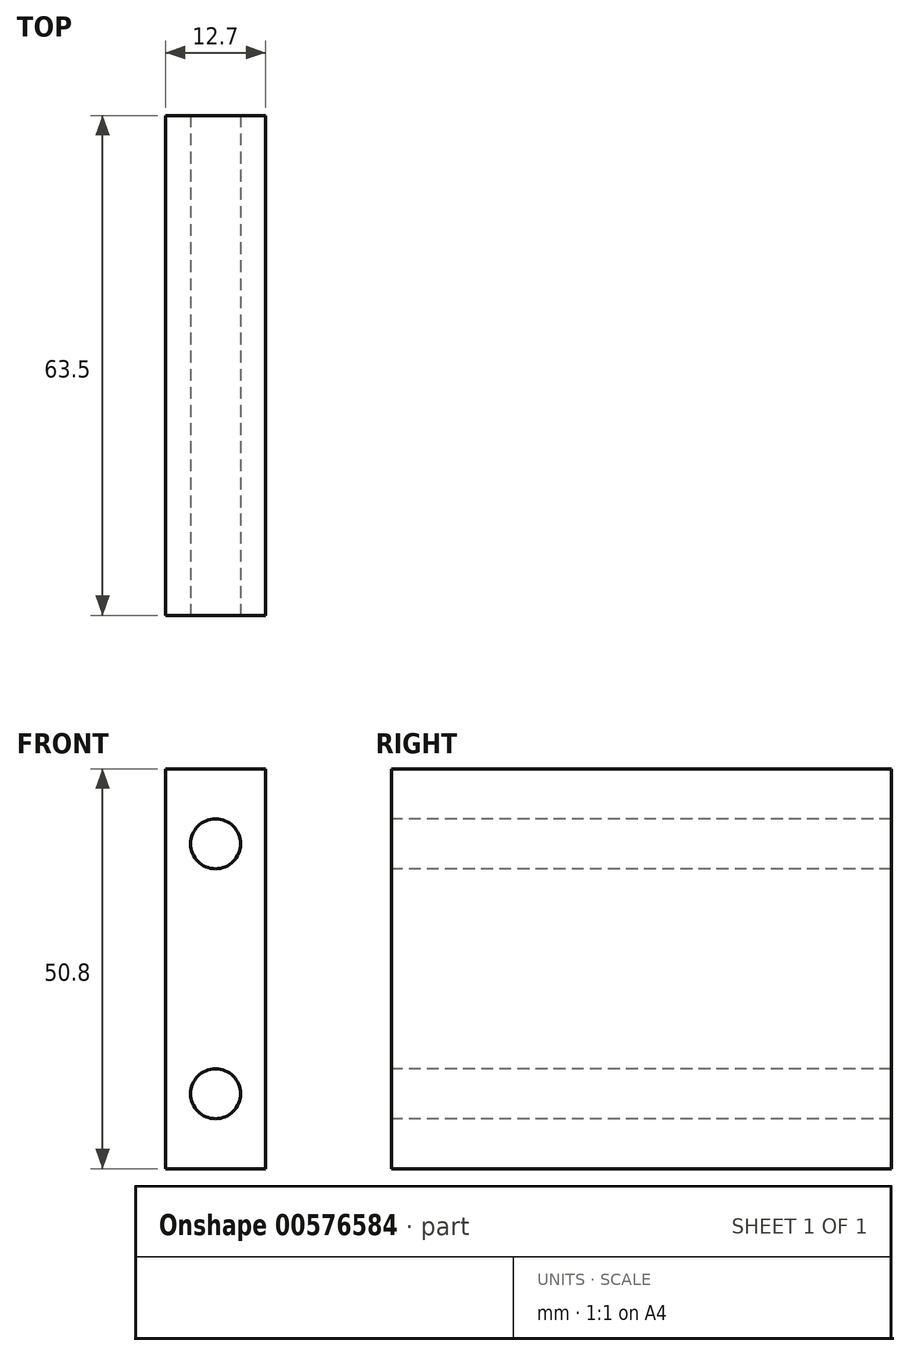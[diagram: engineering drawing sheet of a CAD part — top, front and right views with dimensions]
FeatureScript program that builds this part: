
annotation { "Feature Type Name" : "Feature", "Feature Type Description" : "" }
export const myFeature = defineFeature(function(context is Context, id is Id, definition is map)
    precondition{}
    {
        {
            var Q0;
            Q0=qCreatedBy(makeId("Right.planeOp"),FACE);
            var sketch = newSketch(context, id + "F0", { "sketchPlane" : qUnion([Q0])});
            skLineSegment(sketch, "E0.bottom", {"start": v(-31.75, 25.4) * mm, "end": v(31.75, 25.4) * mm});
            skLineSegment(sketch, "E0.top", {"start": v(-31.75, -25.4) * mm, "end": v(31.75, -25.4) * mm});
            skLineSegment(sketch, "E0.left", {"start": v(-31.75, 25.4) * mm, "end": v(-31.75, -25.4) * mm});
            skLineSegment(sketch, "E0.right", {"start": v(31.75, 25.4) * mm, "end": v(31.75, -25.4) * mm});
            skPoint(sketch, "E0.middle", {"position": v(0, 0) * mm});
            skSolve(sketch);
        }
        {
            var Q0;
            Q0=makeQuery(id+"F0.imprint","IMPRINT",FACE,{"disambiguationData":[TD([[makeQuery(id+"F0.imprint","IMPRINT",EDGE,{"derivedFrom":sQuery(id+"F0.wireOp",EDGE,"E0.bottom")}),-1.0]])]});
            extrude(context, id + "F1", {"entities" : qUnion([Q0]), "depth" : 12.7 * mm, "offsetDistance" : 25.4 * mm});
        }
        {
            var Q0;
            Q0=makeQuery(id+"F1.opExtrude","SWEPT_FACE",FACE,{"disambiguationData":[OSD([sQuery(id+"F0.wireOp",EDGE,"E0.left")])]});
            var sketch = newSketch(context, id + "F2", { "sketchPlane" : qUnion([Q0])});
            skPoint(sketch, "E1", {"position": v(6.35, 15.88) * mm});
            skPoint(sketch, "E1.positionSnap0", {"position": v(6.35, 25.4) * mm});
            skPoint(sketch, "E2", {"position": v(6.35, -15.88) * mm});
            skSolve(sketch);
        }
        {
            var Q0;
            Q0=sQuery(id+"F2.wireOp",VERTEX,"E1");
            var Q1;
            Q1=sQuery(id+"F2.wireOp",VERTEX,"E2");
            var Q2;
            Q2=makeQuery(id+"F1.opExtrude","SWEPT_BODY",BODY,{"disambiguationData":[OSD([sQuery(id+"F0.wireOp",EDGE,"E0.bottom"),sQuery(id+"F0.wireOp",EDGE,"E0.top"),sQuery(id+"F0.wireOp",EDGE,"E0.left"),sQuery(id+"F0.wireOp",EDGE,"E0.right")])]});
            hole(context, id + "F3", {"style" : HoleStyle.SIMPLE, "endStyle" : HoleEndStyle.THROUGH, "holeDiameter" : 6.35 * mm, "isTappedThrough" : true, "tappedDepth" : 12.7 * mm, "tapClearance" : 3, "startFromSketch" : true, "locations" : qUnion([Q0, Q1]), "scope" : qUnion([Q2]), "majorDiameter" : 6.35 * mm});
        }
    });
